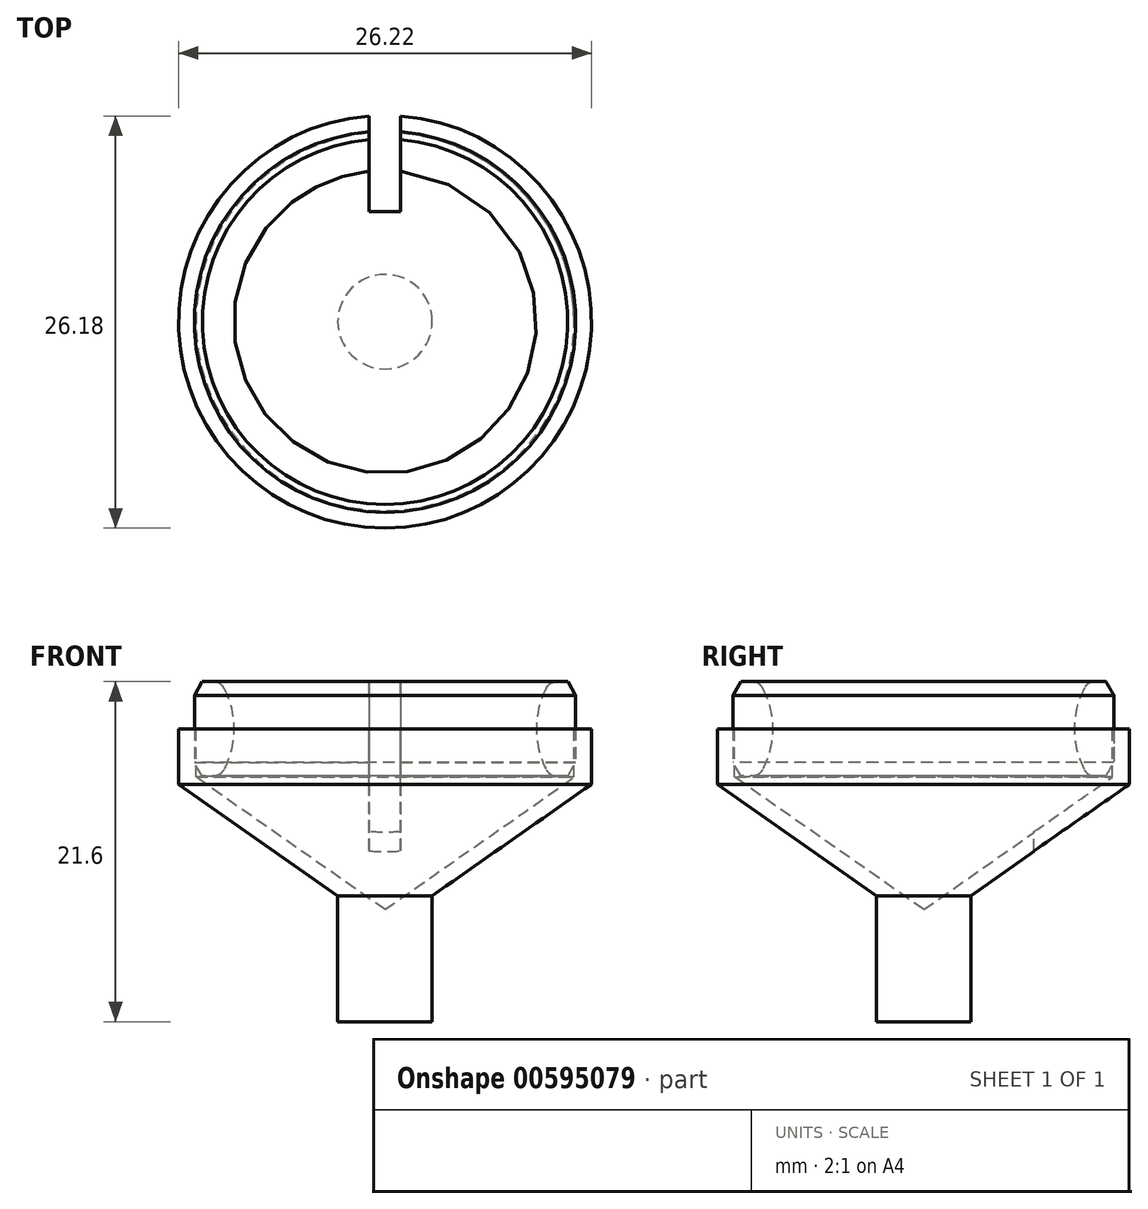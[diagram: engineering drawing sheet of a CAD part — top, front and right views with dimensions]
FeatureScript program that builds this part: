
annotation { "Feature Type Name" : "Feature", "Feature Type Description" : "" }
export const myFeature = defineFeature(function(context is Context, id is Id, definition is map)
    precondition{}
    {
        {
            var Q0;
            Q0=qCreatedBy(makeId("Front.planeOp"),FACE);
            var sketch = newSketch(context, id + "F0", { "sketchPlane" : qUnion([Q0])});
            skLineSegment(sketch, "E0", {"start": v(0, 0) * mm, "end": v(0, 17.87) * mm, "construction": true});
            skArc(sketch, "E1", {"start": v(10.24, 5.6) * mm, "mid": v(9.61, 3) * mm, "end": v(10.24, 0.4) * mm});
            skLineSegment(sketch, "E2", {"start": v(10.9, 0) * mm, "end": v(11.61, 0) * mm});
            skLineSegment(sketch, "E3", {"start": v(11.61, 0) * mm, "end": v(12.1, 0.87) * mm});
            skLineSegment(sketch, "E4", {"start": v(12.11, 0.87) * mm, "end": v(12.11, 5.13) * mm});
            skLineSegment(sketch, "E5", {"start": v(12.11, 5.13) * mm, "end": v(11.61, 6) * mm});
            skLineSegment(sketch, "E6", {"start": v(11.61, 6) * mm, "end": v(10.91, 6) * mm});
            skLineSegment(sketch, "E7", {"start": v(12.11, 3) * mm, "end": v(15.24, 3) * mm, "construction": true});
            skPoint(sketch, "E8.visualSharp", {"position": v(10.48, 6) * mm});
            skArc(sketch, "E8.filletArc", {"start": v(10.91, 6) * mm, "mid": v(10.52, 5.9) * mm, "end": v(10.24, 5.6) * mm});
            skPoint(sketch, "E9.visualSharp", {"position": v(10.48, 0) * mm});
            skArc(sketch, "E9.filletArc", {"start": v(10.24, 0.4) * mm, "mid": v(10.52, 0.1) * mm, "end": v(10.9, 0) * mm});
            skLineSegment(sketch, "E10", {"start": v(10.91, 6) * mm, "end": v(10.9, 0) * mm});
            skSolve(sketch);
        }
        {
            var Q0;
            Q0=makeQuery(id+"F0.imprint","IMPRINT",FACE,{"disambiguationData":[TD([[makeQuery(id+"F0.imprint","IMPRINT",EDGE,{"derivedFrom":sQuery(id+"F0.wireOp",EDGE,"E1")}),1.0]])]});
            var Q1;
            Q1=sQuery(id+"F0.wireOp",EDGE,"E0");
            revolve(context, id + "F1", {"entities" : qUnion([Q0]), "axis" : qUnion([Q1]), "revolveType" : RevolveType.FULL});
        }
        {
            var Q0;
            Q0=makeQuery(id+"F0.imprint","IMPRINT",FACE,{"disambiguationData":[TD([[makeQuery(id+"F0.imprint","IMPRINT",EDGE,{"derivedFrom":sQuery(id+"F0.wireOp",EDGE,"E2")}),1.0]])]});
            var Q1;
            Q1=sQuery(id+"F0.wireOp",EDGE,"E0");
            revolve(context, id + "F2", {"operationType" : NewBodyOperationType.ADD, "entities" : qUnion([Q0]), "axis" : qUnion([Q1]), "revolveType" : RevolveType.FULL});
        }
        {
            var Q0;
            Q0=qCreatedBy(makeId("Front.planeOp"),FACE);
            cPlane(context, id + "F3", {"entities" : qUnion([Q0]), "cplaneType" : CPlaneType.OFFSET, "offset" : 25 * mm, "width" : 150 * mm, "height" : 150 * mm});
        }
        {
            var Q0;
            Q0=qCreatedBy(id+"F3.planeOp",FACE);
            var sketch = newSketch(context, id + "F4", { "sketchPlane" : qUnion([Q0])});
            skText(sketch, "E11", { "text": "9.25", "fontName": "OpenSans-Regular.ttf"});
            skLineSegment(sketch, "E12", {"start": v(-4.83, 3) * mm, "end": v(0, 3) * mm, "construction": true});
            const initialGuessF4  = {"E11": [-0.00483, 0.00125, 1, 0, 0.0035]};
            skSetInitialGuess(sketch, initialGuessF4);
            skSolve(sketch);
        }
        {
            var Q0;
            Q0=qCreatedBy(makeId("Front.planeOp"),FACE);
            var sketch = newSketch(context, id + "F5", { "sketchPlane" : qUnion([Q0])});
            skLineSegment(sketch, "E13", {"start": v(12.11, 0) * mm, "end": v(12.11, 3) * mm, "construction": true});
            skLineSegment(sketch, "E14.0", {"start": v(0, 0) * mm, "end": v(0, 17.87) * mm, "construction": true});
            skLineSegment(sketch, "E15", {"start": v(0, -15.6) * mm, "end": v(3, -15.6) * mm});
            skLineSegment(sketch, "E16", {"start": v(3, -15.6) * mm, "end": v(3, -7.6) * mm});
            skPoint(sketch, "E17.orphan", {"position": v(12.1, 0.87) * mm});
            skLineSegment(sketch, "E18", {"start": v(0, -8.48) * mm, "end": v(0, -15.6) * mm});
            skLineSegment(sketch, "E19.0", {"start": v(12, 3) * mm, "end": v(13.1, 3) * mm});
            skLineSegment(sketch, "E20", {"start": v(13.1, 3) * mm, "end": v(13.1, -0.52) * mm});
            skLineSegment(sketch, "E21", {"start": v(12, -0.07) * mm, "end": v(0, -8.48) * mm});
            skLineSegment(sketch, "E22", {"start": v(3, -7.6) * mm, "end": v(13.1, -0.52) * mm});
            skLineSegment(sketch, "E23", {"start": v(12, 3) * mm, "end": v(12, -0.07) * mm});
            skSolve(sketch);
        }
        {
            var Q0;
            Q0=makeQuery(id+"F5.imprint","IMPRINT",FACE,{"disambiguationData":[TD([[makeQuery(id+"F5.imprint","IMPRINT",EDGE,{"derivedFrom":sQuery(id+"F5.wireOp",EDGE,"E15")}),1.0]])]});
            var Q1;
            Q1=sQuery(id+"F5.wireOp",EDGE,"E18");
            revolve(context, id + "F6", {"entities" : qUnion([Q0]), "axis" : qUnion([Q1]), "revolveType" : RevolveType.FULL});
        }
        {
            var Q0;
            Q0=qCreatedBy(makeId("Top.planeOp"),FACE);
            var sketch = newSketch(context, id + "F7", { "sketchPlane" : qUnion([Q0])});
            skLineSegment(sketch, "E24.bottom", {"start": v(-1, 17) * mm, "end": v(1, 17) * mm});
            skLineSegment(sketch, "E24.top", {"start": v(-1, 7) * mm, "end": v(1, 7) * mm});
            skLineSegment(sketch, "E24.left", {"start": v(-1, 17) * mm, "end": v(-1, 7) * mm});
            skLineSegment(sketch, "E24.right", {"start": v(1, 17) * mm, "end": v(1, 7) * mm});
            skSolve(sketch);
        }
        {
            var Q0;
            Q0=makeQuery(id+"F7.imprint","IMPRINT",FACE,{"disambiguationData":[TD([[makeQuery(id+"F7.imprint","IMPRINT",EDGE,{"derivedFrom":sQuery(id+"F7.wireOp",EDGE,"E24.bottom")}),-1.0]])]});
            extrude(context, id + "F8", {"entities" : qUnion([Q0]), "operationType" : NewBodyOperationType.REMOVE, "oppositeDirection" : true, "depth" : 25 * mm, "offsetDistance" : 25 * mm, "hasSecondDirection" : true, "secondDirectionOppositeDirection" : false, "secondDirectionDepth" : 25 * mm});
        }
    });
